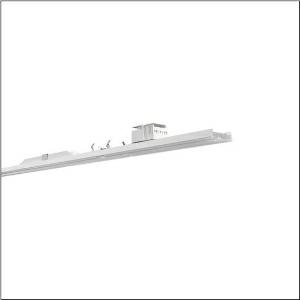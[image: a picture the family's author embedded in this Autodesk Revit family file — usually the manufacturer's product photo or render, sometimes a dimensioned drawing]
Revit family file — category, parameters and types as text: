
# Revit family: licross_r__11_recessed_mo_51tl12dv475f_def5
name_source: partatom
category: Lighting Fixtures
units: mm (PartAtom-declared; Revit-internal decimal feet)

## family parameters
Cut with Voids When Loaded = No
Host = Face
Light Source = No
Part Type = Normal
Room Calculation Point = No
Round Connector Dimension = Use Diameter
Shared = No

## types (1)
- --- (1 x LED, 7640 lm, 42.1 W, 4000K)
    Apparent Load = 42 VA
    CIE Flux Codes = 67 92 99 100 100
    Color Rendering = 80
    Color Temperature = 4000K
    Default Elevation = 1800 mm
    Description = Licross® 11 Recessed MOluminaire insert, length: 2.250mm, width: 66mm, height: 67mm, LED rated luminous flux: 7.640lm, light colour: 840, control gear: DALI 2, control gear: ECG DALI, with plug, 5-pole, with phase selection, mains connection: 220..240V, AC, 50/60Hz, halogen-free wiring, primary optical cover: cover, of PMMA, light emission: direct distribution, protection rating (complete): IP40, insulation class (complete): insulation class I (protective earthing), certification: CE, ENEC, VDE, protection symbol: D if used in an environment without relevant dust loads with corresponding accessories, permissible ambient temperature for indoor applications: -25..+45°C, corresponds to IFS (International Featured Standards) requirements for safety and quality in the food industry, reducing of maximum allowable ambient temperature of 5°C with ceiling mounting, packaging unit: 1 piece
    Height = 58 mm
    Lamp = 1 x LED
    Lamp Light Flux = 7640 lm
    Lamp Power = 42.1 W
    Lamp count = 1
    Length = 2250 mm
    Luminous efficacy = 181 lm/W
    Manufacturer = Siteco
    ModVariant = No
    Model = 51TL12DV475F
    Mounting Place = Ceiling
    Mounting Type = Pendant
    Number of Poles = 1
    OnlyDefault = Yes
    Power Factor = 1
    Product Name = Licross® 11 Recessed MO
    Product group = luminaire insert
    ProductGroupID = 902
    Protection Class = Protection class I
    Protection Degree = IP 40
    RLX_Detail_Level = 1
    RlxData = <blob elided: 27025 chars, md5=b97c0674>
    Socket = socket
    Standby Power = 0 W
    System Light Flux = 7640 lm
    System Power = 42 W
    Type Comments = factory setting: luminous flux: 100 % | dim-lin: 254 | 190 mA
    Type Image = l_1266722.jpg
    URL = http://relux.com
    VarID = @adj_133246
    Voltage = 0 V
    Weight = 0.00 kg
    Width = 66 mm

## geometry (parser evidence)
native form markers: Blend x4, Sweep x11
no freeform markers — native parametric forms only
